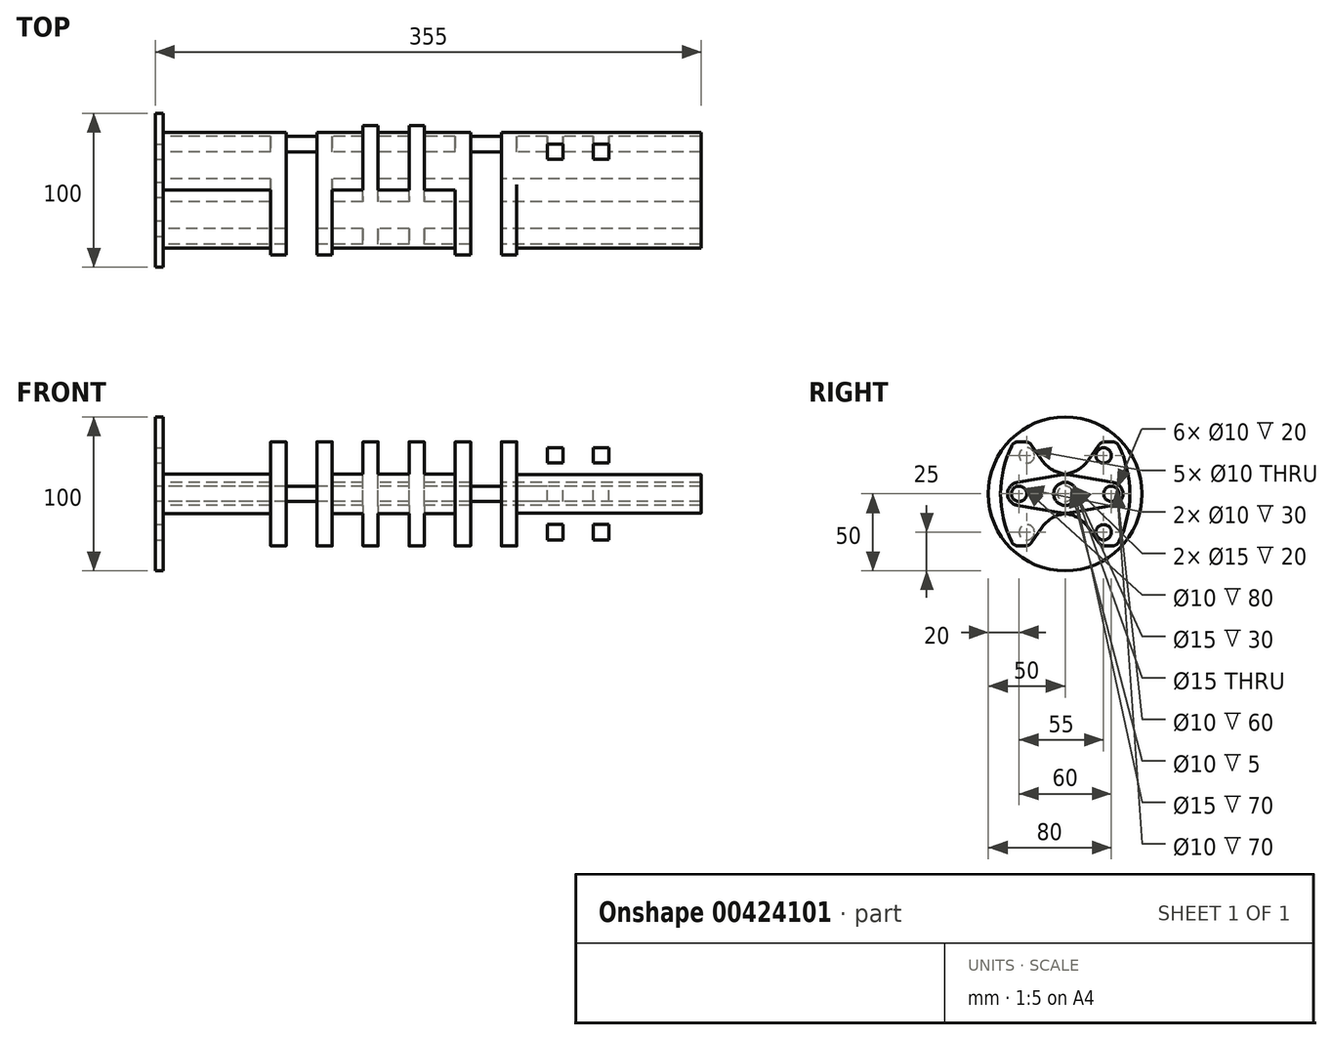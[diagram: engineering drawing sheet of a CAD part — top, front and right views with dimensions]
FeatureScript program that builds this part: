
annotation { "Feature Type Name" : "Feature", "Feature Type Description" : "" }
export const myFeature = defineFeature(function(context is Context, id is Id, definition is map)
    precondition{}
    {
        {
            var Q0;
            Q0=qCreatedBy(makeId("Right.planeOp"),FACE);
            var sketch = newSketch(context, id + "F0", { "sketchPlane" : qUnion([Q0])});
            skCircle(sketch, "E0", {"center": v(0, 0) * mm, "radius": 7.5 * mm});
            skCircle(sketch, "E1", {"center": v(30, 0) * mm, "radius": 5 * mm});
            skArc(sketch, "E2", {"start": v(31.3, 7.39) * mm, "mid": v(37.5, 0) * mm, "end": v(31.3, -7.39) * mm});
            skLineSegment(sketch, "E3", {"start": v(31.3, 7.39) * mm, "end": v(-10, 14.67) * mm});
            skLineSegment(sketch, "E4", {"start": v(31.3, -7.39) * mm, "end": v(-10, -14.67) * mm});
            skPoint(sketch, "E5", {"position": v(37.5, 0) * mm});
            skLineSegment(sketch, "E6", {"start": v(31.3, 7.39) * mm, "end": v(30, 0) * mm, "construction": true});
            skLineSegment(sketch, "E7", {"start": v(31.3, -7.39) * mm, "end": v(30, 0) * mm, "construction": true});
            skArc(sketch, "E8", {"start": v(-33.5, 33.94) * mm, "mid": v(-42, 0) * mm, "end": v(-33.5, -33.94) * mm});
            skLineSegment(sketch, "E9", {"start": v(-33.5, 33.94) * mm, "end": v(-23.5, 33.94) * mm});
            skLineSegment(sketch, "E10", {"start": v(-23.5, 33.94) * mm, "end": v(-10, 14.67) * mm});
            skLineSegment(sketch, "E11", {"start": v(-33.5, -33.94) * mm, "end": v(-23.5, -33.94) * mm});
            skLineSegment(sketch, "E12", {"start": v(-23.5, -33.94) * mm, "end": v(-10, -14.67) * mm});
            skLineSegment(sketch, "E13", {"start": v(0, 0) * mm, "end": v(0, 34.38) * mm, "construction": true});
            skLineSegment(sketch, "E14.MirrorCS", {"start": v(-31.3, -7.39) * mm, "end": v(-30, 0) * mm, "construction": true});
            skLineSegment(sketch, "E15.MirrorCS", {"start": v(23.5, 33.94) * mm, "end": v(10, 14.67) * mm});
            skLineSegment(sketch, "E16.MirrorCS", {"start": v(33.5, -33.94) * mm, "end": v(23.5, -33.94) * mm});
            skLineSegment(sketch, "E17.MirrorCS", {"start": v(-31.3, -7.39) * mm, "end": v(10, -14.67) * mm});
            skArc(sketch, "E18.MirrorCS", {"start": v(33.5, 33.94) * mm, "mid": v(42, 0) * mm, "end": v(33.5, -33.94) * mm});
            skLineSegment(sketch, "E19.MirrorCS", {"start": v(23.5, -33.94) * mm, "end": v(10, -14.67) * mm});
            skLineSegment(sketch, "E20.MirrorCS", {"start": v(-31.3, 7.39) * mm, "end": v(-30, 0) * mm, "construction": true});
            skLineSegment(sketch, "E21.MirrorCS", {"start": v(-31.3, 7.39) * mm, "end": v(10, 14.67) * mm});
            skCircle(sketch, "E22.MirrorC", {"center": v(-30, 0) * mm, "radius": 5 * mm});
            skArc(sketch, "E23.MirrorCS", {"start": v(-31.3, 7.39) * mm, "mid": v(-37.5, 0) * mm, "end": v(-31.3, -7.39) * mm});
            skPoint(sketch, "E24.MirrorP", {"position": v(-37.5, 0) * mm});
            skLineSegment(sketch, "E25.MirrorCS", {"start": v(33.5, 33.94) * mm, "end": v(23.5, 33.94) * mm});
            skCircle(sketch, "E26", {"center": v(0, 0) * mm, "radius": 50 * mm});
            skCircle(sketch, "E27", {"center": v(25, 25) * mm, "radius": 5 * mm});
            skCircle(sketch, "E28", {"center": v(-25, 25) * mm, "radius": 5 * mm});
            skCircle(sketch, "E29", {"center": v(-25, -25) * mm, "radius": 5 * mm});
            skCircle(sketch, "E30", {"center": v(25, -25) * mm, "radius": 5 * mm});
            skLineSegment(sketch, "E31.bottom", {"start": v(-25, 25) * mm, "end": v(25, 25) * mm, "construction": true});
            skLineSegment(sketch, "E31.top", {"start": v(-25, -25) * mm, "end": v(25, -25) * mm, "construction": true});
            skLineSegment(sketch, "E31.left", {"start": v(-25, 25) * mm, "end": v(-25, -25) * mm, "construction": true});
            skLineSegment(sketch, "E31.right", {"start": v(25, 25) * mm, "end": v(25, -25) * mm, "construction": true});
            skSolve(sketch);
        }
        {
            var Q0;
            Q0=makeQuery(id+"F0.imprint","IMPRINT",FACE,{"disambiguationData":[TD([[makeQuery(id+"F0.imprint","IMPRINT",EDGE,{"derivedFrom":sQuery(id+"F0.wireOp",EDGE,"E0")}),-1.0]])]});
            extrude(context, id + "F1", {"entities" : qUnion([Q0]), "depth" : 70 * mm});
        }
        {
            var Q0;
            {var subQ0=sQuery(id+"F0.wireOp",EDGE,"E9");Q0=makeQuery(id+"F0.imprint","IMPRINT",FACE,{"disambiguationData":[TD([[makeQuery(id+"F0.imprint","IMPRINT",EDGE,{"derivedFrom":subQ0}),-1.0]])]});}
            var Q1;
            Q1=makeQuery(id+"F0.imprint","IMPRINT",FACE,{"disambiguationData":[TD([[makeQuery(id+"F0.imprint","IMPRINT",EDGE,{"derivedFrom":sQuery(id+"F0.wireOp",EDGE,"E0")}),1.0]])]});
            var Q2;
            {var subQ0=sQuery(id+"F0.wireOp",EDGE,"E11");Q2=makeQuery(id+"F0.imprint","IMPRINT",FACE,{"disambiguationData":[TD([[makeQuery(id+"F0.imprint","IMPRINT",EDGE,{"derivedFrom":subQ0}),1.0]])]});}
            var Q3;
            {var subQ6=sQuery(id+"F0.wireOp",EDGE,"E1");Q3=makeQuery(id+"F0.imprint","IMPRINT",FACE,{"disambiguationData":[TD([[makeQuery(id+"F0.imprint","IMPRINT",EDGE,{"derivedFrom":subQ6}),-1.0]])]});}
            var Q4;
            Q4=makeQuery(id+"F0.imprint","IMPRINT",FACE,{"disambiguationData":[TD([[makeQuery(id+"F0.imprint","IMPRINT",EDGE,{"derivedFrom":sQuery(id+"F0.wireOp",EDGE,"E1")}),1.0]])]});
            var Q5;
            Q5=makeQuery(id+"F0.imprint","IMPRINT",FACE,{"disambiguationData":[TD([[makeQuery(id+"F0.imprint","IMPRINT",EDGE,{"derivedFrom":sQuery(id+"F0.wireOp",EDGE,"E0")}),-1.0]])]});
            var Q6;
            Q6=makeQuery(id+"F0.imprint","IMPRINT",FACE,{"disambiguationData":[TD([[makeQuery(id+"F0.imprint","IMPRINT",EDGE,{"derivedFrom":sQuery(id+"F0.wireOp",EDGE,"E28")}),1.0]])]});
            var Q7;
            Q7=makeQuery(id+"F0.imprint","IMPRINT",FACE,{"disambiguationData":[TD([[makeQuery(id+"F0.imprint","IMPRINT",EDGE,{"derivedFrom":sQuery(id+"F0.wireOp",EDGE,"E29")}),1.0]])]});
            var Q8;
            Q8=makeQuery(id+"F0.imprint","IMPRINT",FACE,{"disambiguationData":[TD([[makeQuery(id+"F0.imprint","IMPRINT",EDGE,{"derivedFrom":sQuery(id+"F0.wireOp",EDGE,"E22.MirrorC")}),-1.0]])]});
            var Q9;
            Q9=makeQuery(id+"F1.opExtrude","CAP_FACE",FACE,{"disambiguationData":[OSD([sQuery(id+"F0.wireOp",EDGE,"E0")])],"isStart":false});
            extrude(context, id + "F2", {"entities" : qUnion([Q0, Q1, Q2, Q3, Q4, Q5, Q6, Q7, Q8]), "operationType" : NewBodyOperationType.ADD, "depth" : 80 * mm, "hasSecondDirection" : true, "secondDirectionBound" : SecondDirectionBoundingType.UP_TO_SURFACE, "secondDirectionOppositeDirection" : false, "secondDirectionBoundEntityFace" : qUnion([Q9]), "secondDirectionDepth" : 20 * mm});
        }
        {
            var Q0;
            Q0=makeQuery(id+"F0.imprint","IMPRINT",FACE,{"disambiguationData":[TD([[makeQuery(id+"F0.imprint","IMPRINT",EDGE,{"derivedFrom":sQuery(id+"F0.wireOp",EDGE,"E1")}),1.0]])]});
            var Q1;
            Q1=makeQuery(id+"F2.opExtrude","CAP_FACE",FACE,{"disambiguationData":[OSD([sQuery(id+"F0.wireOp",EDGE,"E2"),sQuery(id+"F0.wireOp",EDGE,"E3"),sQuery(id+"F0.wireOp",EDGE,"E4"),sQuery(id+"F0.wireOp",EDGE,"E8"),sQuery(id+"F0.wireOp",EDGE,"E9"),sQuery(id+"F0.wireOp",EDGE,"E10"),sQuery(id+"F0.wireOp",EDGE,"E11"),sQuery(id+"F0.wireOp",EDGE,"E12")])],"isStart":false});
            extrude(context, id + "F3", {"entities" : qUnion([Q0]), "operationType" : NewBodyOperationType.ADD, "depth" : 100 * mm, "hasSecondDirection" : true, "secondDirectionBound" : SecondDirectionBoundingType.UP_TO_SURFACE, "secondDirectionOppositeDirection" : false, "secondDirectionBoundEntityFace" : qUnion([Q1]), "secondDirectionDepth" : 30 * mm});
        }
        {
            var Q0;
            {var subQ0=sQuery(id+"F0.wireOp",EDGE,"E9");Q0=makeQuery(id+"F0.imprint","IMPRINT",FACE,{"disambiguationData":[TD([[makeQuery(id+"F0.imprint","IMPRINT",EDGE,{"derivedFrom":subQ0}),-1.0]])]});}
            var Q1;
            Q1=makeQuery(id+"F0.imprint","IMPRINT",FACE,{"disambiguationData":[TD([[makeQuery(id+"F0.imprint","IMPRINT",EDGE,{"derivedFrom":sQuery(id+"F0.wireOp",EDGE,"E0")}),1.0]])]});
            var Q2;
            {var subQ0=sQuery(id+"F0.wireOp",EDGE,"E11");Q2=makeQuery(id+"F0.imprint","IMPRINT",FACE,{"disambiguationData":[TD([[makeQuery(id+"F0.imprint","IMPRINT",EDGE,{"derivedFrom":subQ0}),1.0]])]});}
            var Q3;
            {var subQ6=sQuery(id+"F0.wireOp",EDGE,"E1");Q3=makeQuery(id+"F0.imprint","IMPRINT",FACE,{"disambiguationData":[TD([[makeQuery(id+"F0.imprint","IMPRINT",EDGE,{"derivedFrom":subQ6}),-1.0]])]});}
            var Q4;
            Q4=makeQuery(id+"F0.imprint","IMPRINT",FACE,{"disambiguationData":[TD([[makeQuery(id+"F0.imprint","IMPRINT",EDGE,{"derivedFrom":sQuery(id+"F0.wireOp",EDGE,"E1")}),1.0]])]});
            var Q5;
            Q5=makeQuery(id+"F0.imprint","IMPRINT",FACE,{"disambiguationData":[TD([[makeQuery(id+"F0.imprint","IMPRINT",EDGE,{"derivedFrom":sQuery(id+"F0.wireOp",EDGE,"E0")}),-1.0]])]});
            var Q6;
            Q6=makeQuery(id+"F0.imprint","IMPRINT",FACE,{"disambiguationData":[TD([[makeQuery(id+"F0.imprint","IMPRINT",EDGE,{"derivedFrom":sQuery(id+"F0.wireOp",EDGE,"E22.MirrorC")}),-1.0]])]});
            var Q7;
            Q7=makeQuery(id+"F0.imprint","IMPRINT",FACE,{"disambiguationData":[TD([[makeQuery(id+"F0.imprint","IMPRINT",EDGE,{"derivedFrom":sQuery(id+"F0.wireOp",EDGE,"E28")}),1.0]])]});
            var Q8;
            Q8=makeQuery(id+"F0.imprint","IMPRINT",FACE,{"disambiguationData":[TD([[makeQuery(id+"F0.imprint","IMPRINT",EDGE,{"derivedFrom":sQuery(id+"F0.wireOp",EDGE,"E29")}),1.0]])]});
            var Q9;
            Q9=makeQuery(id+"F3.opExtrude","CAP_FACE",FACE,{"disambiguationData":[OSD([sQuery(id+"F0.wireOp",EDGE,"E1")])],"isStart":false});
            extrude(context, id + "F4", {"entities" : qUnion([Q0, Q1, Q2, Q3, Q4, Q5, Q6, Q7, Q8]), "operationType" : NewBodyOperationType.ADD, "depth" : 110 * mm, "hasSecondDirection" : true, "secondDirectionBound" : SecondDirectionBoundingType.UP_TO_SURFACE, "secondDirectionOppositeDirection" : false, "secondDirectionBoundEntityFace" : qUnion([Q9]), "secondDirectionDepth" : 50 * mm});
        }
        {
            var Q0;
            Q0=makeQuery(id+"F0.imprint","IMPRINT",FACE,{"disambiguationData":[TD([[makeQuery(id+"F0.imprint","IMPRINT",EDGE,{"derivedFrom":sQuery(id+"F0.wireOp",EDGE,"E0")}),-1.0]])]});
            var Q1;
            Q1=makeQuery(id+"F4.opExtrude","CAP_FACE",FACE,{"disambiguationData":[OSD([sQuery(id+"F0.wireOp",EDGE,"E2"),sQuery(id+"F0.wireOp",EDGE,"E3"),sQuery(id+"F0.wireOp",EDGE,"E4"),sQuery(id+"F0.wireOp",EDGE,"E8"),sQuery(id+"F0.wireOp",EDGE,"E9"),sQuery(id+"F0.wireOp",EDGE,"E10"),sQuery(id+"F0.wireOp",EDGE,"E11"),sQuery(id+"F0.wireOp",EDGE,"E12")])],"isStart":false});
            extrude(context, id + "F5", {"entities" : qUnion([Q0]), "operationType" : NewBodyOperationType.ADD, "depth" : 130 * mm, "hasSecondDirection" : true, "secondDirectionBound" : SecondDirectionBoundingType.UP_TO_SURFACE, "secondDirectionOppositeDirection" : false, "secondDirectionBoundEntityFace" : qUnion([Q1]), "secondDirectionDepth" : 60 * mm});
        }
        {
            var Q0;
            {var subQ1=sQuery(id+"F0.wireOp",EDGE,"E15.MirrorCS");Q0=makeQuery(id+"F0.imprint","IMPRINT",FACE,{"disambiguationData":[TD([[makeQuery(id+"F0.imprint","IMPRINT",EDGE,{"derivedFrom":subQ1}),1.0]])]});}
            var Q1;
            Q1=makeQuery(id+"F0.imprint","IMPRINT",FACE,{"disambiguationData":[TD([[makeQuery(id+"F0.imprint","IMPRINT",EDGE,{"derivedFrom":sQuery(id+"F0.wireOp",EDGE,"E0")}),1.0]])]});
            var Q2;
            {var subQ1=sQuery(id+"F0.wireOp",EDGE,"E16.MirrorCS");Q2=makeQuery(id+"F0.imprint","IMPRINT",FACE,{"disambiguationData":[TD([[makeQuery(id+"F0.imprint","IMPRINT",EDGE,{"derivedFrom":subQ1}),-1.0]])]});}
            var Q3;
            {var subQ4=sQuery(id+"F0.wireOp",EDGE,"E22.MirrorC");Q3=makeQuery(id+"F0.imprint","IMPRINT",FACE,{"disambiguationData":[TD([[makeQuery(id+"F0.imprint","IMPRINT",EDGE,{"derivedFrom":subQ4}),1.0]])]});}
            var Q4;
            Q4=makeQuery(id+"F0.imprint","IMPRINT",FACE,{"disambiguationData":[TD([[makeQuery(id+"F0.imprint","IMPRINT",EDGE,{"derivedFrom":sQuery(id+"F0.wireOp",EDGE,"E22.MirrorC")}),-1.0]])]});
            var Q5;
            Q5=makeQuery(id+"F0.imprint","IMPRINT",FACE,{"disambiguationData":[TD([[makeQuery(id+"F0.imprint","IMPRINT",EDGE,{"derivedFrom":sQuery(id+"F0.wireOp",EDGE,"E0")}),-1.0]])]});
            var Q6;
            Q6=makeQuery(id+"F0.imprint","IMPRINT",FACE,{"disambiguationData":[TD([[makeQuery(id+"F0.imprint","IMPRINT",EDGE,{"derivedFrom":sQuery(id+"F0.wireOp",EDGE,"E27")}),1.0]])]});
            var Q7;
            Q7=makeQuery(id+"F0.imprint","IMPRINT",FACE,{"disambiguationData":[TD([[makeQuery(id+"F0.imprint","IMPRINT",EDGE,{"derivedFrom":sQuery(id+"F0.wireOp",EDGE,"E1")}),1.0]])]});
            var Q8;
            Q8=makeQuery(id+"F0.imprint","IMPRINT",FACE,{"disambiguationData":[TD([[makeQuery(id+"F0.imprint","IMPRINT",EDGE,{"derivedFrom":sQuery(id+"F0.wireOp",EDGE,"E30")}),1.0]])]});
            var Q9;
            Q9=makeQuery(id+"F5.opExtrude","CAP_FACE",FACE,{"disambiguationData":[OSD([sQuery(id+"F0.wireOp",EDGE,"E0")])],"isStart":false});
            extrude(context, id + "F6", {"entities" : qUnion([Q0, Q1, Q2, Q3, Q4, Q5, Q6, Q7, Q8]), "operationType" : NewBodyOperationType.ADD, "depth" : 140 * mm, "hasSecondDirection" : true, "secondDirectionBound" : SecondDirectionBoundingType.UP_TO_SURFACE, "secondDirectionOppositeDirection" : false, "secondDirectionBoundEntityFace" : qUnion([Q9]), "secondDirectionDepth" : 80 * mm});
        }
        {
            var Q0;
            Q0=makeQuery(id+"F0.imprint","IMPRINT",FACE,{"disambiguationData":[TD([[makeQuery(id+"F0.imprint","IMPRINT",EDGE,{"derivedFrom":sQuery(id+"F0.wireOp",EDGE,"E22.MirrorC")}),-1.0]])]});
            var Q1;
            Q1=makeQuery(id+"F6.opExtrude","CAP_FACE",FACE,{"disambiguationData":[OSD([sQuery(id+"F0.wireOp",EDGE,"E15.MirrorCS"),sQuery(id+"F0.wireOp",EDGE,"E16.MirrorCS"),sQuery(id+"F0.wireOp",EDGE,"E17.MirrorCS"),sQuery(id+"F0.wireOp",EDGE,"E18.MirrorCS"),sQuery(id+"F0.wireOp",EDGE,"E19.MirrorCS"),sQuery(id+"F0.wireOp",EDGE,"E21.MirrorCS"),sQuery(id+"F0.wireOp",EDGE,"E23.MirrorCS"),sQuery(id+"F0.wireOp",EDGE,"E25.MirrorCS")])],"isStart":false});
            extrude(context, id + "F7", {"entities" : qUnion([Q0]), "operationType" : NewBodyOperationType.ADD, "depth" : 160 * mm, "hasSecondDirection" : true, "secondDirectionBound" : SecondDirectionBoundingType.UP_TO_SURFACE, "secondDirectionOppositeDirection" : false, "secondDirectionBoundEntityFace" : qUnion([Q1]), "secondDirectionDepth" : 90 * mm});
        }
        {
            var Q0;
            {var subQ4=sQuery(id+"F0.wireOp",EDGE,"E22.MirrorC");Q0=makeQuery(id+"F0.imprint","IMPRINT",FACE,{"disambiguationData":[TD([[makeQuery(id+"F0.imprint","IMPRINT",EDGE,{"derivedFrom":subQ4}),1.0]])]});}
            var Q1;
            Q1=makeQuery(id+"F0.imprint","IMPRINT",FACE,{"disambiguationData":[TD([[makeQuery(id+"F0.imprint","IMPRINT",EDGE,{"derivedFrom":sQuery(id+"F0.wireOp",EDGE,"E0")}),1.0]])]});
            var Q2;
            {var subQ1=sQuery(id+"F0.wireOp",EDGE,"E15.MirrorCS");Q2=makeQuery(id+"F0.imprint","IMPRINT",FACE,{"disambiguationData":[TD([[makeQuery(id+"F0.imprint","IMPRINT",EDGE,{"derivedFrom":subQ1}),1.0]])]});}
            var Q3;
            Q3=makeQuery(id+"F0.imprint","IMPRINT",FACE,{"disambiguationData":[TD([[makeQuery(id+"F0.imprint","IMPRINT",EDGE,{"derivedFrom":sQuery(id+"F0.wireOp",EDGE,"E22.MirrorC")}),-1.0]])]});
            var Q4;
            Q4=makeQuery(id+"F0.imprint","IMPRINT",FACE,{"disambiguationData":[TD([[makeQuery(id+"F0.imprint","IMPRINT",EDGE,{"derivedFrom":sQuery(id+"F0.wireOp",EDGE,"E0")}),-1.0]])]});
            var Q5;
            {var subQ1=sQuery(id+"F0.wireOp",EDGE,"E16.MirrorCS");Q5=makeQuery(id+"F0.imprint","IMPRINT",FACE,{"disambiguationData":[TD([[makeQuery(id+"F0.imprint","IMPRINT",EDGE,{"derivedFrom":subQ1}),-1.0]])]});}
            var Q6;
            Q6=makeQuery(id+"F0.imprint","IMPRINT",FACE,{"disambiguationData":[TD([[makeQuery(id+"F0.imprint","IMPRINT",EDGE,{"derivedFrom":sQuery(id+"F0.wireOp",EDGE,"E27")}),1.0]])]});
            var Q7;
            Q7=makeQuery(id+"F0.imprint","IMPRINT",FACE,{"disambiguationData":[TD([[makeQuery(id+"F0.imprint","IMPRINT",EDGE,{"derivedFrom":sQuery(id+"F0.wireOp",EDGE,"E1")}),1.0]])]});
            var Q8;
            Q8=makeQuery(id+"F0.imprint","IMPRINT",FACE,{"disambiguationData":[TD([[makeQuery(id+"F0.imprint","IMPRINT",EDGE,{"derivedFrom":sQuery(id+"F0.wireOp",EDGE,"E30")}),1.0]])]});
            var Q9;
            Q9=makeQuery(id+"F7.opExtrude","CAP_FACE",FACE,{"disambiguationData":[OSD([sQuery(id+"F0.wireOp",EDGE,"E22.MirrorC")])],"isStart":false});
            extrude(context, id + "F8", {"entities" : qUnion([Q0, Q1, Q2, Q3, Q4, Q5, Q6, Q7, Q8]), "operationType" : NewBodyOperationType.ADD, "depth" : 170 * mm, "hasSecondDirection" : true, "secondDirectionBound" : SecondDirectionBoundingType.UP_TO_SURFACE, "secondDirectionOppositeDirection" : false, "secondDirectionBoundEntityFace" : qUnion([Q9]), "secondDirectionDepth" : 110 * mm});
        }
        {
            var Q0;
            Q0=makeQuery(id+"F0.imprint","IMPRINT",FACE,{"disambiguationData":[TD([[makeQuery(id+"F0.imprint","IMPRINT",EDGE,{"derivedFrom":sQuery(id+"F0.wireOp",EDGE,"E0")}),-1.0]])]});
            var Q1;
            Q1=makeQuery(id+"F8.opExtrude","CAP_FACE",FACE,{"disambiguationData":[OSD([sQuery(id+"F0.wireOp",EDGE,"E15.MirrorCS"),sQuery(id+"F0.wireOp",EDGE,"E16.MirrorCS"),sQuery(id+"F0.wireOp",EDGE,"E17.MirrorCS"),sQuery(id+"F0.wireOp",EDGE,"E18.MirrorCS"),sQuery(id+"F0.wireOp",EDGE,"E19.MirrorCS"),sQuery(id+"F0.wireOp",EDGE,"E21.MirrorCS"),sQuery(id+"F0.wireOp",EDGE,"E23.MirrorCS"),sQuery(id+"F0.wireOp",EDGE,"E25.MirrorCS")])],"isStart":false});
            extrude(context, id + "F9", {"entities" : qUnion([Q0]), "operationType" : NewBodyOperationType.ADD, "depth" : 190 * mm, "hasSecondDirection" : true, "secondDirectionBound" : SecondDirectionBoundingType.UP_TO_SURFACE, "secondDirectionOppositeDirection" : false, "secondDirectionBoundEntityFace" : qUnion([Q1]), "secondDirectionDepth" : 120 * mm});
        }
        {
            var Q0;
            Q0=makeQuery(id+"F0.imprint","IMPRINT",FACE,{"disambiguationData":[TD([[makeQuery(id+"F0.imprint","IMPRINT",EDGE,{"derivedFrom":sQuery(id+"F0.wireOp",EDGE,"E8")}),1.0]])]});
            var Q1;
            Q1=makeQuery(id+"F0.imprint","IMPRINT",FACE,{"disambiguationData":[TD([[makeQuery(id+"F0.imprint","IMPRINT",EDGE,{"derivedFrom":sQuery(id+"F0.wireOp",EDGE,"E28")}),1.0]])]});
            var Q2;
            Q2=makeQuery(id+"F0.imprint","IMPRINT",FACE,{"disambiguationData":[TD([[makeQuery(id+"F0.imprint","IMPRINT",EDGE,{"derivedFrom":sQuery(id+"F0.wireOp",EDGE,"E22.MirrorC")}),-1.0]])]});
            var Q3;
            Q3=makeQuery(id+"F0.imprint","IMPRINT",FACE,{"disambiguationData":[TD([[makeQuery(id+"F0.imprint","IMPRINT",EDGE,{"derivedFrom":sQuery(id+"F0.wireOp",EDGE,"E29")}),1.0]])]});
            var Q4;
            Q4=makeQuery(id+"F0.imprint","IMPRINT",FACE,{"disambiguationData":[TD([[makeQuery(id+"F0.imprint","IMPRINT",EDGE,{"derivedFrom":sQuery(id+"F0.wireOp",EDGE,"E1")}),-1.0]])]});
            var Q5;
            Q5=makeQuery(id+"F0.imprint","IMPRINT",FACE,{"disambiguationData":[TD([[makeQuery(id+"F0.imprint","IMPRINT",EDGE,{"derivedFrom":sQuery(id+"F0.wireOp",EDGE,"E0")}),-1.0]])]});
            var Q6;
            Q6=makeQuery(id+"F0.imprint","IMPRINT",FACE,{"disambiguationData":[TD([[makeQuery(id+"F0.imprint","IMPRINT",EDGE,{"derivedFrom":sQuery(id+"F0.wireOp",EDGE,"E1")}),1.0]])]});
            var Q7;
            Q7=makeQuery(id+"F9.opExtrude","CAP_FACE",FACE,{"disambiguationData":[OSD([sQuery(id+"F0.wireOp",EDGE,"E0")])],"isStart":false});
            extrude(context, id + "F10", {"entities" : qUnion([Q0, Q1, Q2, Q3, Q4, Q5, Q6]), "operationType" : NewBodyOperationType.ADD, "depth" : 200 * mm, "hasSecondDirection" : true, "secondDirectionBound" : SecondDirectionBoundingType.UP_TO_SURFACE, "secondDirectionOppositeDirection" : false, "secondDirectionBoundEntityFace" : qUnion([Q7]), "secondDirectionDepth" : 25 * mm});
        }
        {
            var Q0;
            Q0=makeQuery(id+"F0.imprint","IMPRINT",FACE,{"disambiguationData":[TD([[makeQuery(id+"F0.imprint","IMPRINT",EDGE,{"derivedFrom":sQuery(id+"F0.wireOp",EDGE,"E1")}),1.0]])]});
            var Q1;
            Q1=makeQuery(id+"F10.opExtrude","CAP_FACE",FACE,{"disambiguationData":[OSD([sQuery(id+"F0.wireOp",EDGE,"E2"),sQuery(id+"F0.wireOp",EDGE,"E3"),sQuery(id+"F0.wireOp",EDGE,"E4"),sQuery(id+"F0.wireOp",EDGE,"E8"),sQuery(id+"F0.wireOp",EDGE,"E9"),sQuery(id+"F0.wireOp",EDGE,"E10"),sQuery(id+"F0.wireOp",EDGE,"E11"),sQuery(id+"F0.wireOp",EDGE,"E12")])],"isStart":false});
            extrude(context, id + "F11", {"entities" : qUnion([Q0]), "operationType" : NewBodyOperationType.ADD, "depth" : 220 * mm, "hasSecondDirection" : true, "secondDirectionBound" : SecondDirectionBoundingType.UP_TO_SURFACE, "secondDirectionOppositeDirection" : false, "secondDirectionBoundEntityFace" : qUnion([Q1]), "secondDirectionDepth" : 25 * mm});
        }
        {
            var Q0;
            Q0=makeQuery(id+"F0.imprint","IMPRINT",FACE,{"disambiguationData":[TD([[makeQuery(id+"F0.imprint","IMPRINT",EDGE,{"derivedFrom":sQuery(id+"F0.wireOp",EDGE,"E1")}),-1.0]])]});
            var Q1;
            Q1=makeQuery(id+"F0.imprint","IMPRINT",FACE,{"disambiguationData":[TD([[makeQuery(id+"F0.imprint","IMPRINT",EDGE,{"derivedFrom":sQuery(id+"F0.wireOp",EDGE,"E1")}),1.0]])]});
            var Q2;
            Q2=makeQuery(id+"F0.imprint","IMPRINT",FACE,{"disambiguationData":[TD([[makeQuery(id+"F0.imprint","IMPRINT",EDGE,{"derivedFrom":sQuery(id+"F0.wireOp",EDGE,"E0")}),-1.0]])]});
            var Q3;
            Q3=makeQuery(id+"F0.imprint","IMPRINT",FACE,{"disambiguationData":[TD([[makeQuery(id+"F0.imprint","IMPRINT",EDGE,{"derivedFrom":sQuery(id+"F0.wireOp",EDGE,"E29")}),1.0]])]});
            var Q4;
            Q4=makeQuery(id+"F0.imprint","IMPRINT",FACE,{"disambiguationData":[TD([[makeQuery(id+"F0.imprint","IMPRINT",EDGE,{"derivedFrom":sQuery(id+"F0.wireOp",EDGE,"E8")}),1.0]])]});
            var Q5;
            Q5=makeQuery(id+"F0.imprint","IMPRINT",FACE,{"disambiguationData":[TD([[makeQuery(id+"F0.imprint","IMPRINT",EDGE,{"derivedFrom":sQuery(id+"F0.wireOp",EDGE,"E22.MirrorC")}),-1.0]])]});
            var Q6;
            Q6=makeQuery(id+"F0.imprint","IMPRINT",FACE,{"disambiguationData":[TD([[makeQuery(id+"F0.imprint","IMPRINT",EDGE,{"derivedFrom":sQuery(id+"F0.wireOp",EDGE,"E28")}),1.0]])]});
            var Q7;
            Q7=makeQuery(id+"F11.opExtrude","CAP_FACE",FACE,{"disambiguationData":[OSD([sQuery(id+"F0.wireOp",EDGE,"E1")])],"isStart":false});
            extrude(context, id + "F12", {"entities" : qUnion([Q0, Q1, Q2, Q3, Q4, Q5, Q6]), "operationType" : NewBodyOperationType.ADD, "depth" : 230 * mm, "hasSecondDirection" : true, "secondDirectionBound" : SecondDirectionBoundingType.UP_TO_SURFACE, "secondDirectionOppositeDirection" : false, "secondDirectionBoundEntityFace" : qUnion([Q7]), "secondDirectionDepth" : 25 * mm});
        }
        {
            var Q0;
            Q0=makeQuery(id+"F0.imprint","IMPRINT",FACE,{"disambiguationData":[TD([[makeQuery(id+"F0.imprint","IMPRINT",EDGE,{"derivedFrom":sQuery(id+"F0.wireOp",EDGE,"E0")}),-1.0]])]});
            var Q1;
            Q1=makeQuery(id+"F12.opExtrude","CAP_FACE",FACE,{"disambiguationData":[OSD([sQuery(id+"F0.wireOp",EDGE,"E2"),sQuery(id+"F0.wireOp",EDGE,"E3"),sQuery(id+"F0.wireOp",EDGE,"E4"),sQuery(id+"F0.wireOp",EDGE,"E8"),sQuery(id+"F0.wireOp",EDGE,"E9"),sQuery(id+"F0.wireOp",EDGE,"E10"),sQuery(id+"F0.wireOp",EDGE,"E11"),sQuery(id+"F0.wireOp",EDGE,"E12")])],"isStart":false});
            extrude(context, id + "F13", {"entities" : qUnion([Q0]), "operationType" : NewBodyOperationType.ADD, "depth" : 250 * mm, "hasSecondDirection" : true, "secondDirectionBound" : SecondDirectionBoundingType.UP_TO_SURFACE, "secondDirectionOppositeDirection" : false, "secondDirectionBoundEntityFace" : qUnion([Q1]), "secondDirectionDepth" : 25 * mm});
        }
        {
            var Q0;
            Q0=makeQuery(id+"F0.imprint","IMPRINT",FACE,{"disambiguationData":[TD([[makeQuery(id+"F0.imprint","IMPRINT",EDGE,{"derivedFrom":sQuery(id+"F0.wireOp",EDGE,"E1")}),1.0]])]});
            var Q1;
            {var subQ5=sQuery(id+"F0.wireOp",EDGE,"E2");Q1=makeQuery(id+"F0.imprint","IMPRINT",FACE,{"disambiguationData":[TD([[makeQuery(id+"F0.imprint","IMPRINT",EDGE,{"derivedFrom":subQ5}),1.0]])]});}
            var Q2;
            Q2=makeQuery(id+"F0.imprint","IMPRINT",FACE,{"disambiguationData":[TD([[makeQuery(id+"F0.imprint","IMPRINT",EDGE,{"derivedFrom":sQuery(id+"F0.wireOp",EDGE,"E27")}),1.0]])]});
            var Q3;
            Q3=makeQuery(id+"F0.imprint","IMPRINT",FACE,{"disambiguationData":[TD([[makeQuery(id+"F0.imprint","IMPRINT",EDGE,{"derivedFrom":sQuery(id+"F0.wireOp",EDGE,"E30")}),1.0]])]});
            var Q4;
            Q4=makeQuery(id+"F0.imprint","IMPRINT",FACE,{"disambiguationData":[TD([[makeQuery(id+"F0.imprint","IMPRINT",EDGE,{"derivedFrom":sQuery(id+"F0.wireOp",EDGE,"E1")}),-1.0]])]});
            var Q5;
            Q5=makeQuery(id+"F0.imprint","IMPRINT",FACE,{"disambiguationData":[TD([[makeQuery(id+"F0.imprint","IMPRINT",EDGE,{"derivedFrom":sQuery(id+"F0.wireOp",EDGE,"E22.MirrorC")}),-1.0]])]});
            var Q6;
            Q6=makeQuery(id+"F0.imprint","IMPRINT",FACE,{"disambiguationData":[TD([[makeQuery(id+"F0.imprint","IMPRINT",EDGE,{"derivedFrom":sQuery(id+"F0.wireOp",EDGE,"E0")}),-1.0]])]});
            var Q7;
            Q7=makeQuery(id+"F13.opExtrude","CAP_FACE",FACE,{"disambiguationData":[OSD([sQuery(id+"F0.wireOp",EDGE,"E0")])],"isStart":false});
            extrude(context, id + "F14", {"entities" : qUnion([Q0, Q1, Q2, Q3, Q4, Q5, Q6]), "operationType" : NewBodyOperationType.ADD, "depth" : 260 * mm, "hasSecondDirection" : true, "secondDirectionBound" : SecondDirectionBoundingType.UP_TO_SURFACE, "secondDirectionOppositeDirection" : false, "secondDirectionBoundEntityFace" : qUnion([Q7]), "secondDirectionDepth" : 25 * mm});
        }
        {
            var Q0;
            Q0=makeQuery(id+"F0.imprint","IMPRINT",FACE,{"disambiguationData":[TD([[makeQuery(id+"F0.imprint","IMPRINT",EDGE,{"derivedFrom":sQuery(id+"F0.wireOp",EDGE,"E22.MirrorC")}),-1.0]])]});
            var Q1;
            Q1=makeQuery(id+"F14.opExtrude","CAP_FACE",FACE,{"disambiguationData":[OSD([sQuery(id+"F0.wireOp",EDGE,"E15.MirrorCS"),sQuery(id+"F0.wireOp",EDGE,"E16.MirrorCS"),sQuery(id+"F0.wireOp",EDGE,"E17.MirrorCS"),sQuery(id+"F0.wireOp",EDGE,"E18.MirrorCS"),sQuery(id+"F0.wireOp",EDGE,"E19.MirrorCS"),sQuery(id+"F0.wireOp",EDGE,"E21.MirrorCS"),sQuery(id+"F0.wireOp",EDGE,"E23.MirrorCS"),sQuery(id+"F0.wireOp",EDGE,"E25.MirrorCS")])],"isStart":false});
            extrude(context, id + "F15", {"entities" : qUnion([Q0]), "operationType" : NewBodyOperationType.ADD, "depth" : 280 * mm, "hasSecondDirection" : true, "secondDirectionBound" : SecondDirectionBoundingType.UP_TO_SURFACE, "secondDirectionOppositeDirection" : false, "secondDirectionBoundEntityFace" : qUnion([Q1]), "secondDirectionDepth" : 25 * mm});
        }
        {
            var Q0;
            Q0=makeQuery(id+"F0.imprint","IMPRINT",FACE,{"disambiguationData":[TD([[makeQuery(id+"F0.imprint","IMPRINT",EDGE,{"derivedFrom":sQuery(id+"F0.wireOp",EDGE,"E1")}),-1.0]])]});
            var Q1;
            {var subQ5=sQuery(id+"F0.wireOp",EDGE,"E2");Q1=makeQuery(id+"F0.imprint","IMPRINT",FACE,{"disambiguationData":[TD([[makeQuery(id+"F0.imprint","IMPRINT",EDGE,{"derivedFrom":subQ5}),1.0]])]});}
            var Q2;
            Q2=makeQuery(id+"F0.imprint","IMPRINT",FACE,{"disambiguationData":[TD([[makeQuery(id+"F0.imprint","IMPRINT",EDGE,{"derivedFrom":sQuery(id+"F0.wireOp",EDGE,"E30")}),1.0]])]});
            var Q3;
            Q3=makeQuery(id+"F0.imprint","IMPRINT",FACE,{"disambiguationData":[TD([[makeQuery(id+"F0.imprint","IMPRINT",EDGE,{"derivedFrom":sQuery(id+"F0.wireOp",EDGE,"E1")}),1.0]])]});
            var Q4;
            Q4=makeQuery(id+"F0.imprint","IMPRINT",FACE,{"disambiguationData":[TD([[makeQuery(id+"F0.imprint","IMPRINT",EDGE,{"derivedFrom":sQuery(id+"F0.wireOp",EDGE,"E27")}),1.0]])]});
            var Q5;
            Q5=makeQuery(id+"F0.imprint","IMPRINT",FACE,{"disambiguationData":[TD([[makeQuery(id+"F0.imprint","IMPRINT",EDGE,{"derivedFrom":sQuery(id+"F0.wireOp",EDGE,"E0")}),-1.0]])]});
            var Q6;
            Q6=makeQuery(id+"F0.imprint","IMPRINT",FACE,{"disambiguationData":[TD([[makeQuery(id+"F0.imprint","IMPRINT",EDGE,{"derivedFrom":sQuery(id+"F0.wireOp",EDGE,"E22.MirrorC")}),-1.0]])]});
            var Q7;
            Q7=makeQuery(id+"F15.opExtrude","CAP_FACE",FACE,{"disambiguationData":[OSD([sQuery(id+"F0.wireOp",EDGE,"E22.MirrorC")])],"isStart":false});
            extrude(context, id + "F16", {"entities" : qUnion([Q0, Q1, Q2, Q3, Q4, Q5, Q6]), "operationType" : NewBodyOperationType.ADD, "depth" : 290 * mm, "hasSecondDirection" : true, "secondDirectionBound" : SecondDirectionBoundingType.UP_TO_SURFACE, "secondDirectionOppositeDirection" : false, "secondDirectionBoundEntityFace" : qUnion([Q7]), "secondDirectionDepth" : 25 * mm});
        }
        {
            var Q0;
            Q0=makeQuery(id+"F0.imprint","IMPRINT",FACE,{"disambiguationData":[TD([[makeQuery(id+"F0.imprint","IMPRINT",EDGE,{"derivedFrom":sQuery(id+"F0.wireOp",EDGE,"E0")}),-1.0]])]});
            var Q1;
            Q1=makeQuery(id+"F16.opExtrude","CAP_FACE",FACE,{"disambiguationData":[OSD([sQuery(id+"F0.wireOp",EDGE,"E15.MirrorCS"),sQuery(id+"F0.wireOp",EDGE,"E16.MirrorCS"),sQuery(id+"F0.wireOp",EDGE,"E17.MirrorCS"),sQuery(id+"F0.wireOp",EDGE,"E18.MirrorCS"),sQuery(id+"F0.wireOp",EDGE,"E19.MirrorCS"),sQuery(id+"F0.wireOp",EDGE,"E21.MirrorCS"),sQuery(id+"F0.wireOp",EDGE,"E23.MirrorCS"),sQuery(id+"F0.wireOp",EDGE,"E25.MirrorCS")])],"isStart":false});
            extrude(context, id + "F17", {"entities" : qUnion([Q0]), "operationType" : NewBodyOperationType.ADD, "depth" : 350 * mm, "hasSecondDirection" : true, "secondDirectionBound" : SecondDirectionBoundingType.UP_TO_SURFACE, "secondDirectionOppositeDirection" : false, "secondDirectionBoundEntityFace" : qUnion([Q1]), "secondDirectionDepth" : 25 * mm});
        }
        {
            var Q0;
            Q0=makeQuery(id+"F2.opExtrude","SWEPT_EDGE",EDGE,{"disambiguationData":[OSD([sQuery(id+"F0.wireOp",EDGE,"E3"),sQuery(id+"F0.wireOp",EDGE,"E10")])]});
            var Q1;
            Q1=makeQuery(id+"F4.opExtrude","SWEPT_EDGE",EDGE,{"disambiguationData":[OSD([sQuery(id+"F0.wireOp",EDGE,"E3"),sQuery(id+"F0.wireOp",EDGE,"E10")])]});
            var Q2;
            Q2=makeQuery(id+"F6.opExtrude","SWEPT_EDGE",EDGE,{"disambiguationData":[OSD([sQuery(id+"F0.wireOp",EDGE,"E15.MirrorCS"),sQuery(id+"F0.wireOp",EDGE,"E21.MirrorCS")])]});
            var Q3;
            Q3=makeQuery(id+"F8.opExtrude","SWEPT_EDGE",EDGE,{"disambiguationData":[OSD([sQuery(id+"F0.wireOp",EDGE,"E15.MirrorCS"),sQuery(id+"F0.wireOp",EDGE,"E21.MirrorCS")])]});
            var Q4;
            Q4=makeQuery(id+"F8.opExtrude","SWEPT_EDGE",EDGE,{"disambiguationData":[OSD([sQuery(id+"F0.wireOp",EDGE,"E17.MirrorCS"),sQuery(id+"F0.wireOp",EDGE,"E19.MirrorCS")])]});
            var Q5;
            Q5=makeQuery(id+"F6.opExtrude","SWEPT_EDGE",EDGE,{"disambiguationData":[OSD([sQuery(id+"F0.wireOp",EDGE,"E17.MirrorCS"),sQuery(id+"F0.wireOp",EDGE,"E19.MirrorCS")])]});
            var Q6;
            Q6=makeQuery(id+"F2.opExtrude","SWEPT_EDGE",EDGE,{"disambiguationData":[OSD([sQuery(id+"F0.wireOp",EDGE,"E4"),sQuery(id+"F0.wireOp",EDGE,"E12")])]});
            var Q7;
            Q7=makeQuery(id+"F4.opExtrude","SWEPT_EDGE",EDGE,{"disambiguationData":[OSD([sQuery(id+"F0.wireOp",EDGE,"E4"),sQuery(id+"F0.wireOp",EDGE,"E12")])]});
            var Q8;
            Q8=makeQuery(id+"F10.opExtrude","SWEPT_EDGE",EDGE,{"disambiguationData":[OSD([sQuery(id+"F0.wireOp",EDGE,"E3"),sQuery(id+"F0.wireOp",EDGE,"E10")])]});
            var Q9;
            Q9=makeQuery(id+"F12.opExtrude","SWEPT_EDGE",EDGE,{"disambiguationData":[OSD([sQuery(id+"F0.wireOp",EDGE,"E3"),sQuery(id+"F0.wireOp",EDGE,"E10")])]});
            var Q10;
            Q10=makeQuery(id+"F14.opExtrude","SWEPT_EDGE",EDGE,{"disambiguationData":[OSD([sQuery(id+"F0.wireOp",EDGE,"E15.MirrorCS"),sQuery(id+"F0.wireOp",EDGE,"E21.MirrorCS")])]});
            var Q11;
            Q11=makeQuery(id+"F16.opExtrude","SWEPT_EDGE",EDGE,{"disambiguationData":[OSD([sQuery(id+"F0.wireOp",EDGE,"E15.MirrorCS"),sQuery(id+"F0.wireOp",EDGE,"E21.MirrorCS")])]});
            var Q12;
            Q12=makeQuery(id+"F10.opExtrude","SWEPT_EDGE",EDGE,{"disambiguationData":[OSD([sQuery(id+"F0.wireOp",EDGE,"E4"),sQuery(id+"F0.wireOp",EDGE,"E12")])]});
            var Q13;
            Q13=makeQuery(id+"F12.opExtrude","SWEPT_EDGE",EDGE,{"disambiguationData":[OSD([sQuery(id+"F0.wireOp",EDGE,"E4"),sQuery(id+"F0.wireOp",EDGE,"E12")])]});
            var Q14;
            Q14=makeQuery(id+"F14.opExtrude","SWEPT_EDGE",EDGE,{"disambiguationData":[OSD([sQuery(id+"F0.wireOp",EDGE,"E17.MirrorCS"),sQuery(id+"F0.wireOp",EDGE,"E19.MirrorCS")])]});
            var Q15;
            Q15=makeQuery(id+"F16.opExtrude","SWEPT_EDGE",EDGE,{"disambiguationData":[OSD([sQuery(id+"F0.wireOp",EDGE,"E17.MirrorCS"),sQuery(id+"F0.wireOp",EDGE,"E19.MirrorCS")])]});
            fillet(context, id + "F18", {"entities" : qUnion([Q0, Q1, Q2, Q3, Q4, Q5, Q6, Q7, Q8, Q9, Q10, Q11, Q12, Q13, Q14, Q15]), "radius" : 20 * mm, "tangentPropagation" : true, "allowEdgeOverflow" : false});
        }
        {
            var Q0;
            Q0=makeQuery(id+"F2.opExtrude","SWEPT_EDGE",EDGE,{"disambiguationData":[OSD([sQuery(id+"F0.wireOp",EDGE,"E8"),sQuery(id+"F0.wireOp",EDGE,"E9")])]});
            var Q1;
            Q1=makeQuery(id+"F2.opExtrude","SWEPT_EDGE",EDGE,{"disambiguationData":[OSD([sQuery(id+"F0.wireOp",EDGE,"E9"),sQuery(id+"F0.wireOp",EDGE,"E10")])]});
            var Q2;
            Q2=makeQuery(id+"F4.opExtrude","SWEPT_EDGE",EDGE,{"disambiguationData":[OSD([sQuery(id+"F0.wireOp",EDGE,"E8"),sQuery(id+"F0.wireOp",EDGE,"E9")])]});
            var Q3;
            Q3=makeQuery(id+"F4.opExtrude","SWEPT_EDGE",EDGE,{"disambiguationData":[OSD([sQuery(id+"F0.wireOp",EDGE,"E9"),sQuery(id+"F0.wireOp",EDGE,"E10")])]});
            var Q4;
            Q4=makeQuery(id+"F6.opExtrude","SWEPT_EDGE",EDGE,{"disambiguationData":[OSD([sQuery(id+"F0.wireOp",EDGE,"E15.MirrorCS"),sQuery(id+"F0.wireOp",EDGE,"E25.MirrorCS")])]});
            var Q5;
            Q5=makeQuery(id+"F6.opExtrude","SWEPT_EDGE",EDGE,{"disambiguationData":[OSD([sQuery(id+"F0.wireOp",EDGE,"E18.MirrorCS"),sQuery(id+"F0.wireOp",EDGE,"E25.MirrorCS")])]});
            var Q6;
            Q6=makeQuery(id+"F8.opExtrude","SWEPT_EDGE",EDGE,{"disambiguationData":[OSD([sQuery(id+"F0.wireOp",EDGE,"E15.MirrorCS"),sQuery(id+"F0.wireOp",EDGE,"E25.MirrorCS")])]});
            var Q7;
            Q7=makeQuery(id+"F8.opExtrude","SWEPT_EDGE",EDGE,{"disambiguationData":[OSD([sQuery(id+"F0.wireOp",EDGE,"E18.MirrorCS"),sQuery(id+"F0.wireOp",EDGE,"E25.MirrorCS")])]});
            var Q8;
            Q8=makeQuery(id+"F2.opExtrude","SWEPT_EDGE",EDGE,{"disambiguationData":[OSD([sQuery(id+"F0.wireOp",EDGE,"E11"),sQuery(id+"F0.wireOp",EDGE,"E12")])]});
            var Q9;
            Q9=makeQuery(id+"F2.opExtrude","SWEPT_EDGE",EDGE,{"disambiguationData":[OSD([sQuery(id+"F0.wireOp",EDGE,"E8"),sQuery(id+"F0.wireOp",EDGE,"E11")])]});
            var Q10;
            Q10=makeQuery(id+"F4.opExtrude","SWEPT_EDGE",EDGE,{"disambiguationData":[OSD([sQuery(id+"F0.wireOp",EDGE,"E8"),sQuery(id+"F0.wireOp",EDGE,"E11")])]});
            var Q11;
            Q11=makeQuery(id+"F4.opExtrude","SWEPT_EDGE",EDGE,{"disambiguationData":[OSD([sQuery(id+"F0.wireOp",EDGE,"E11"),sQuery(id+"F0.wireOp",EDGE,"E12")])]});
            var Q12;
            Q12=makeQuery(id+"F6.opExtrude","SWEPT_EDGE",EDGE,{"disambiguationData":[OSD([sQuery(id+"F0.wireOp",EDGE,"E16.MirrorCS"),sQuery(id+"F0.wireOp",EDGE,"E19.MirrorCS")])]});
            var Q13;
            Q13=makeQuery(id+"F6.opExtrude","SWEPT_EDGE",EDGE,{"disambiguationData":[OSD([sQuery(id+"F0.wireOp",EDGE,"E16.MirrorCS"),sQuery(id+"F0.wireOp",EDGE,"E18.MirrorCS")])]});
            var Q14;
            Q14=makeQuery(id+"F8.opExtrude","SWEPT_EDGE",EDGE,{"disambiguationData":[OSD([sQuery(id+"F0.wireOp",EDGE,"E16.MirrorCS"),sQuery(id+"F0.wireOp",EDGE,"E19.MirrorCS")])]});
            var Q15;
            Q15=makeQuery(id+"F8.opExtrude","SWEPT_EDGE",EDGE,{"disambiguationData":[OSD([sQuery(id+"F0.wireOp",EDGE,"E16.MirrorCS"),sQuery(id+"F0.wireOp",EDGE,"E18.MirrorCS")])]});
            var Q16;
            Q16=makeQuery(id+"F10.opExtrude","SWEPT_EDGE",EDGE,{"disambiguationData":[OSD([sQuery(id+"F0.wireOp",EDGE,"E9"),sQuery(id+"F0.wireOp",EDGE,"E10")])]});
            var Q17;
            Q17=makeQuery(id+"F10.opExtrude","SWEPT_EDGE",EDGE,{"disambiguationData":[OSD([sQuery(id+"F0.wireOp",EDGE,"E8"),sQuery(id+"F0.wireOp",EDGE,"E9")])]});
            var Q18;
            Q18=makeQuery(id+"F12.opExtrude","SWEPT_EDGE",EDGE,{"disambiguationData":[OSD([sQuery(id+"F0.wireOp",EDGE,"E9"),sQuery(id+"F0.wireOp",EDGE,"E10")])]});
            var Q19;
            Q19=makeQuery(id+"F12.opExtrude","SWEPT_EDGE",EDGE,{"disambiguationData":[OSD([sQuery(id+"F0.wireOp",EDGE,"E8"),sQuery(id+"F0.wireOp",EDGE,"E9")])]});
            var Q20;
            Q20=makeQuery(id+"F14.opExtrude","SWEPT_EDGE",EDGE,{"disambiguationData":[OSD([sQuery(id+"F0.wireOp",EDGE,"E18.MirrorCS"),sQuery(id+"F0.wireOp",EDGE,"E25.MirrorCS")])]});
            var Q21;
            Q21=makeQuery(id+"F14.opExtrude","SWEPT_EDGE",EDGE,{"disambiguationData":[OSD([sQuery(id+"F0.wireOp",EDGE,"E15.MirrorCS"),sQuery(id+"F0.wireOp",EDGE,"E25.MirrorCS")])]});
            var Q22;
            Q22=makeQuery(id+"F16.opExtrude","SWEPT_EDGE",EDGE,{"disambiguationData":[OSD([sQuery(id+"F0.wireOp",EDGE,"E15.MirrorCS"),sQuery(id+"F0.wireOp",EDGE,"E25.MirrorCS")])]});
            var Q23;
            Q23=makeQuery(id+"F16.opExtrude","SWEPT_EDGE",EDGE,{"disambiguationData":[OSD([sQuery(id+"F0.wireOp",EDGE,"E18.MirrorCS"),sQuery(id+"F0.wireOp",EDGE,"E25.MirrorCS")])]});
            var Q24;
            Q24=makeQuery(id+"F16.opExtrude","SWEPT_EDGE",EDGE,{"disambiguationData":[OSD([sQuery(id+"F0.wireOp",EDGE,"E16.MirrorCS"),sQuery(id+"F0.wireOp",EDGE,"E19.MirrorCS")])]});
            var Q25;
            Q25=makeQuery(id+"F16.opExtrude","SWEPT_EDGE",EDGE,{"disambiguationData":[OSD([sQuery(id+"F0.wireOp",EDGE,"E16.MirrorCS"),sQuery(id+"F0.wireOp",EDGE,"E18.MirrorCS")])]});
            var Q26;
            Q26=makeQuery(id+"F14.opExtrude","SWEPT_EDGE",EDGE,{"disambiguationData":[OSD([sQuery(id+"F0.wireOp",EDGE,"E16.MirrorCS"),sQuery(id+"F0.wireOp",EDGE,"E18.MirrorCS")])]});
            var Q27;
            Q27=makeQuery(id+"F14.opExtrude","SWEPT_EDGE",EDGE,{"disambiguationData":[OSD([sQuery(id+"F0.wireOp",EDGE,"E16.MirrorCS"),sQuery(id+"F0.wireOp",EDGE,"E19.MirrorCS")])]});
            var Q28;
            Q28=makeQuery(id+"F10.opExtrude","SWEPT_EDGE",EDGE,{"disambiguationData":[OSD([sQuery(id+"F0.wireOp",EDGE,"E8"),sQuery(id+"F0.wireOp",EDGE,"E11")])]});
            var Q29;
            Q29=makeQuery(id+"F10.opExtrude","SWEPT_EDGE",EDGE,{"disambiguationData":[OSD([sQuery(id+"F0.wireOp",EDGE,"E11"),sQuery(id+"F0.wireOp",EDGE,"E12")])]});
            var Q30;
            Q30=makeQuery(id+"F12.opExtrude","SWEPT_EDGE",EDGE,{"disambiguationData":[OSD([sQuery(id+"F0.wireOp",EDGE,"E8"),sQuery(id+"F0.wireOp",EDGE,"E11")])]});
            var Q31;
            Q31=makeQuery(id+"F12.opExtrude","SWEPT_EDGE",EDGE,{"disambiguationData":[OSD([sQuery(id+"F0.wireOp",EDGE,"E11"),sQuery(id+"F0.wireOp",EDGE,"E12")])]});
            fillet(context, id + "F19", {"entities" : qUnion([Q0, Q1, Q2, Q3, Q4, Q5, Q6, Q7, Q8, Q9, Q10, Q11, Q12, Q13, Q14, Q15, Q16, Q17, Q18, Q19, Q20, Q21, Q22, Q23, Q24, Q25, Q26, Q27, Q28, Q29, Q30, Q31]), "radius" : 5 * mm, "tangentPropagation" : true, "allowEdgeOverflow" : false});
        }
        {
            var Q0;
            {var subQ16=sQuery(id+"F0.wireOp",EDGE,"E2");Q0=makeQuery(id+"F0.imprint","IMPRINT",FACE,{"disambiguationData":[TD([[makeQuery(id+"F0.imprint","IMPRINT",EDGE,{"derivedFrom":subQ16}),1.0]])]});}
            var Q1;
            {var subQ0=sQuery(id+"F0.wireOp",EDGE,"E9");Q1=makeQuery(id+"F0.imprint","IMPRINT",FACE,{"disambiguationData":[TD([[makeQuery(id+"F0.imprint","IMPRINT",EDGE,{"derivedFrom":subQ0}),-1.0]])]});}
            var Q2;
            Q2=makeQuery(id+"F0.imprint","IMPRINT",FACE,{"disambiguationData":[TD([[makeQuery(id+"F0.imprint","IMPRINT",EDGE,{"derivedFrom":sQuery(id+"F0.wireOp",EDGE,"E22.MirrorC")}),-1.0]])]});
            var Q3;
            {var subQ4=sQuery(id+"F0.wireOp",EDGE,"E22.MirrorC");Q3=makeQuery(id+"F0.imprint","IMPRINT",FACE,{"disambiguationData":[TD([[makeQuery(id+"F0.imprint","IMPRINT",EDGE,{"derivedFrom":subQ4}),1.0]])]});}
            var Q4;
            Q4=makeQuery(id+"F0.imprint","IMPRINT",FACE,{"disambiguationData":[TD([[makeQuery(id+"F0.imprint","IMPRINT",EDGE,{"derivedFrom":sQuery(id+"F0.wireOp",EDGE,"E0")}),-1.0]])]});
            var Q5;
            Q5=makeQuery(id+"F0.imprint","IMPRINT",FACE,{"disambiguationData":[TD([[makeQuery(id+"F0.imprint","IMPRINT",EDGE,{"derivedFrom":sQuery(id+"F0.wireOp",EDGE,"E0")}),1.0]])]});
            var Q6;
            {var subQ1=sQuery(id+"F0.wireOp",EDGE,"E15.MirrorCS");Q6=makeQuery(id+"F0.imprint","IMPRINT",FACE,{"disambiguationData":[TD([[makeQuery(id+"F0.imprint","IMPRINT",EDGE,{"derivedFrom":subQ1}),1.0]])]});}
            var Q7;
            {var subQ1=sQuery(id+"F0.wireOp",EDGE,"E16.MirrorCS");Q7=makeQuery(id+"F0.imprint","IMPRINT",FACE,{"disambiguationData":[TD([[makeQuery(id+"F0.imprint","IMPRINT",EDGE,{"derivedFrom":subQ1}),-1.0]])]});}
            var Q8;
            {var subQ4=sQuery(id+"F0.wireOp",EDGE,"E1");Q8=makeQuery(id+"F0.imprint","IMPRINT",FACE,{"disambiguationData":[TD([[makeQuery(id+"F0.imprint","IMPRINT",EDGE,{"derivedFrom":subQ4}),-1.0]])]});}
            var Q9;
            Q9=makeQuery(id+"F0.imprint","IMPRINT",FACE,{"disambiguationData":[TD([[makeQuery(id+"F0.imprint","IMPRINT",EDGE,{"derivedFrom":sQuery(id+"F0.wireOp",EDGE,"E1")}),1.0]])]});
            var Q10;
            {var subQ1=sQuery(id+"F0.wireOp",EDGE,"E11");Q10=makeQuery(id+"F0.imprint","IMPRINT",FACE,{"disambiguationData":[TD([[makeQuery(id+"F0.imprint","IMPRINT",EDGE,{"derivedFrom":subQ1}),1.0]])]});}
            var Q11;
            Q11=makeQuery(id+"F0.imprint","IMPRINT",FACE,{"disambiguationData":[TD([[makeQuery(id+"F0.imprint","IMPRINT",EDGE,{"derivedFrom":sQuery(id+"F0.wireOp",EDGE,"E8")}),-1.0]])]});
            extrude(context, id + "F20", {"entities" : qUnion([Q0, Q1, Q2, Q3, Q4, Q5, Q6, Q7, Q8, Q9, Q10, Q11]), "operationType" : NewBodyOperationType.ADD, "oppositeDirection" : true, "depth" : 5 * mm});
        }
        {
            var Q0;
            Q0=makeQuery(id+"F20.opExtrude","CAP_FACE",FACE,{"disambiguationData":[OSD([sQuery(id+"F0.wireOp",EDGE,"E26"),sQuery(id+"F0.wireOp",EDGE,"E27"),sQuery(id+"F0.wireOp",EDGE,"E28"),sQuery(id+"F0.wireOp",EDGE,"E29"),sQuery(id+"F0.wireOp",EDGE,"E30")])],"isStart":false});
            var sketch = newSketch(context, id + "F21", { "sketchPlane" : qUnion([Q0])});
            skCircle(sketch, "E32", {"center": v(0, 0) * mm, "radius": 5 * mm});
            skSolve(sketch);
        }
        {
            var Q0;
            Q0 = qSketchRegion(id + "F21", true);
            extrude(context, id + "F22", {"entities" : qUnion([Q0]), "operationType" : NewBodyOperationType.REMOVE, "oppositeDirection" : true, "depth" : 5 * mm});
        }
    });
